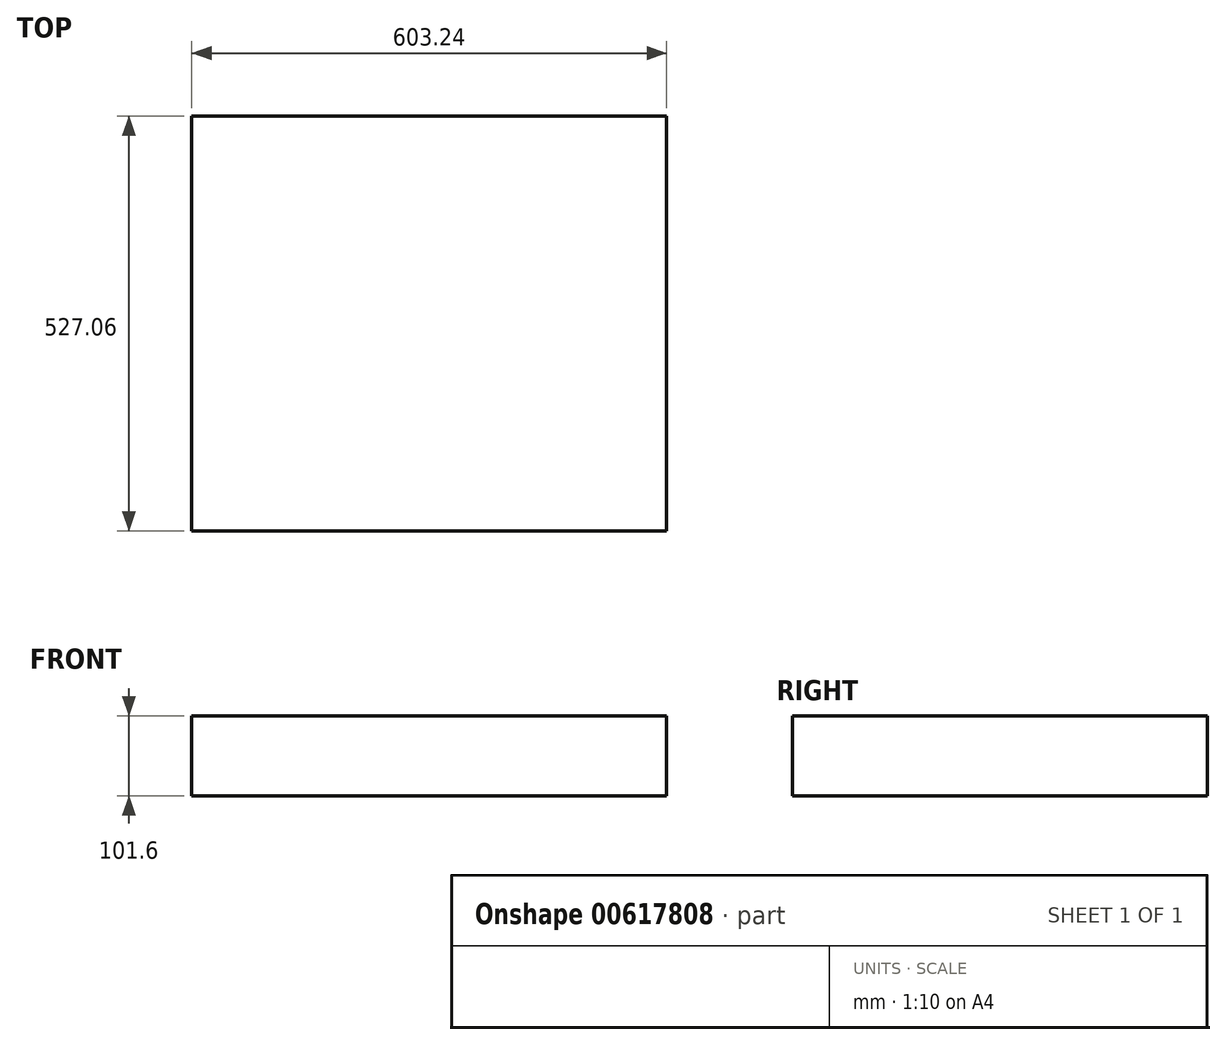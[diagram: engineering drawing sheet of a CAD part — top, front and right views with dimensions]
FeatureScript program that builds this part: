
annotation { "Feature Type Name" : "Feature", "Feature Type Description" : "" }
export const myFeature = defineFeature(function(context is Context, id is Id, definition is map)
    precondition{}
    {
        {
            var Q0;
            Q0=qCreatedBy(makeId("Top.planeOp"),FACE);
            var sketch = newSketch(context, id + "F0", { "sketchPlane" : qUnion([Q0])});
            skLineSegment(sketch, "E0.bottom", {"start": v(-301.62, 263.53) * mm, "end": v(301.63, 263.53) * mm});
            skLineSegment(sketch, "E0.top", {"start": v(-301.63, -263.53) * mm, "end": v(301.62, -263.53) * mm});
            skLineSegment(sketch, "E0.left", {"start": v(-301.62, 263.53) * mm, "end": v(-301.63, -263.53) * mm});
            skLineSegment(sketch, "E0.right", {"start": v(301.63, 263.53) * mm, "end": v(301.62, -263.53) * mm});
            skPoint(sketch, "E0.middle", {"position": v(0, 0) * mm});
            skSolve(sketch);
        }
        {
            var Q0;
            Q0=makeQuery(id+"F0.imprint","IMPRINT",FACE,{"disambiguationData":[TD([[makeQuery(id+"F0.imprint","IMPRINT",EDGE,{"derivedFrom":sQuery(id+"F0.wireOp",EDGE,"E0.bottom")}),-1.0]])]});
            extrude(context, id + "F1", {"entities" : qUnion([Q0]), "depth" : 101.6 * mm, "offsetDistance" : 25.4 * mm});
        }
    });
